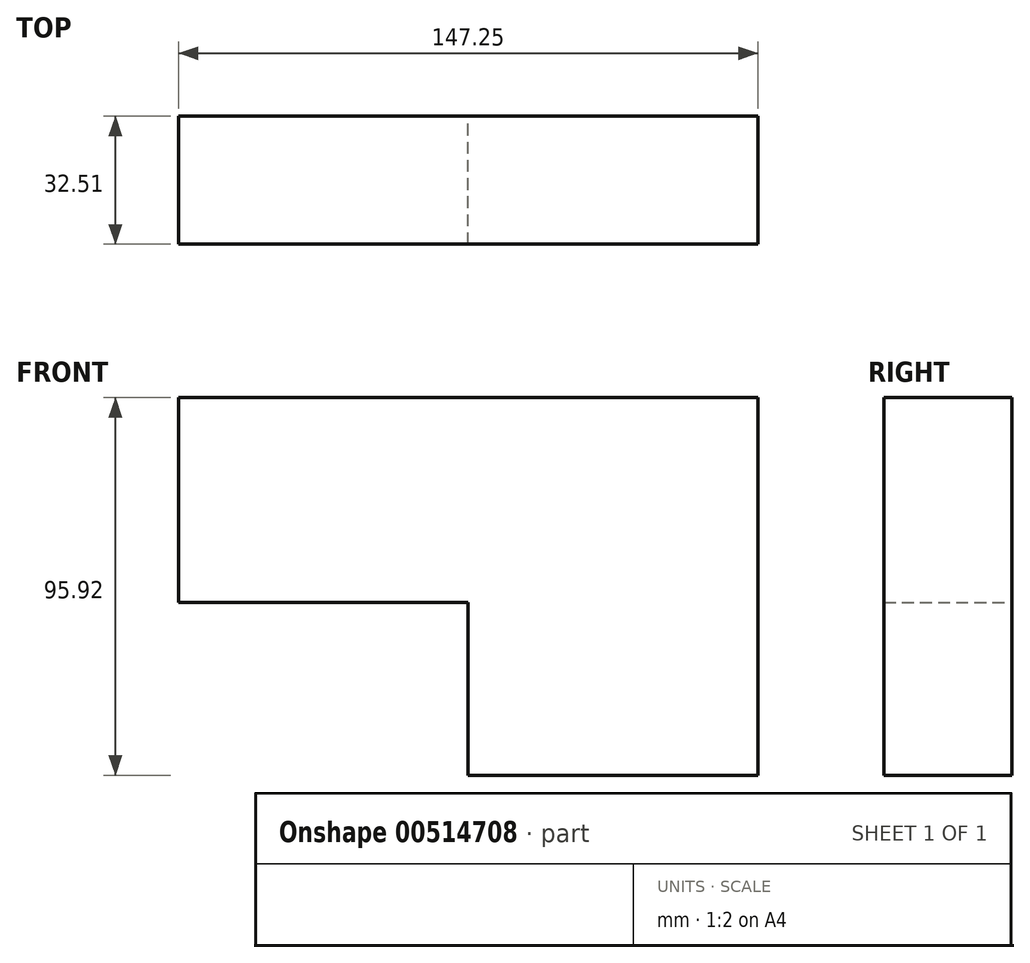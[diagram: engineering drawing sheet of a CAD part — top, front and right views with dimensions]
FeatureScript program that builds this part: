
annotation { "Feature Type Name" : "Feature", "Feature Type Description" : "" }
export const myFeature = defineFeature(function(context is Context, id is Id, definition is map)
    precondition{}
    {
        {
            var Q0;
            Q0=qCreatedBy(makeId("Front.planeOp"),FACE);
            var sketch = newSketch(context, id + "F0", { "sketchPlane" : qUnion([Q0])});
            skLineSegment(sketch, "E0.bottom", {"start": v(-67.48, 58.08) * mm, "end": v(79.77, 58.08) * mm});
            skLineSegment(sketch, "E0.top", {"start": v(-67.48, -37.84) * mm, "end": v(79.77, -37.84) * mm});
            skLineSegment(sketch, "E0.left", {"start": v(-67.48, 58.08) * mm, "end": v(-67.48, -37.84) * mm});
            skLineSegment(sketch, "E0.right", {"start": v(79.77, 58.08) * mm, "end": v(79.77, -37.84) * mm});
            skLineSegment(sketch, "E1", {"start": v(6.15, -37.84) * mm, "end": v(6.15, 6.02) * mm});
            skLineSegment(sketch, "E2", {"start": v(6.15, 6.02) * mm, "end": v(-67.48, 6.02) * mm});
            skSolve(sketch);
        }
        {
            var Q0;
            {var subQ1=sQuery(id+"F0.wireOp",EDGE,"E0.bottom");Q0=makeQuery(id+"F0.imprint","IMPRINT",FACE,{"disambiguationData":[TD([[makeQuery(id+"F0.imprint","IMPRINT",EDGE,{"derivedFrom":subQ1}),-1.0]])]});}
            extrude(context, id + "F1", {"entities" : qUnion([Q0]), "depth" : 32.5 * mm, "offsetDistance" : 25.4 * mm});
        }
    });
